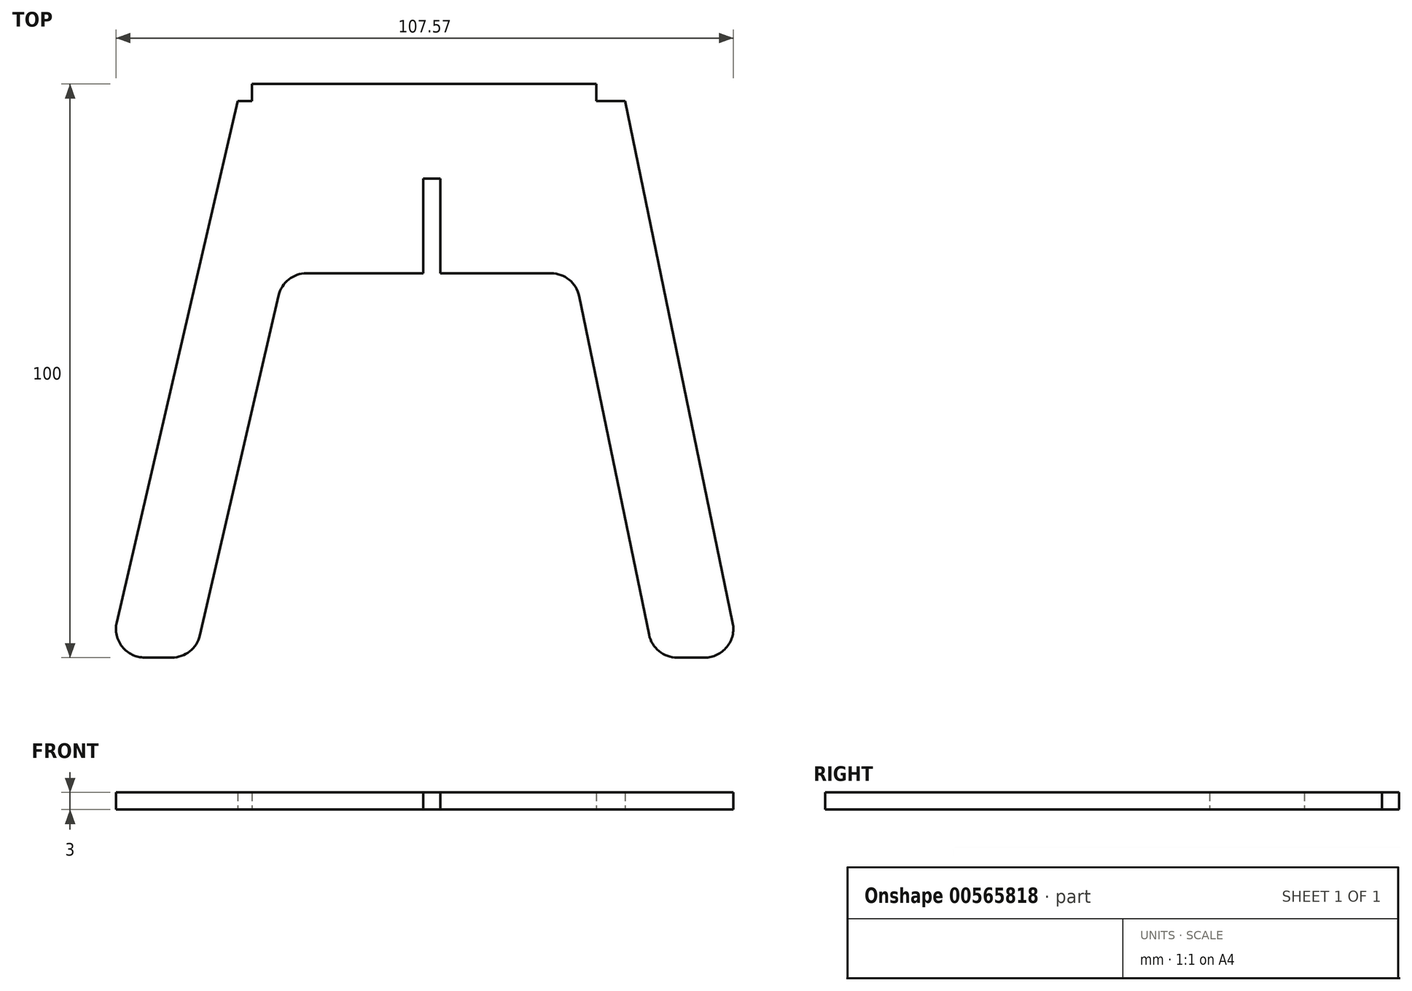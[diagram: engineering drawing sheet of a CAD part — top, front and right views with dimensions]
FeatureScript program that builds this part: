
annotation { "Feature Type Name" : "Feature", "Feature Type Description" : "" }
export const myFeature = defineFeature(function(context is Context, id is Id, definition is map)
    precondition{}
    {
        {
            var Q0;
            Q0=qCreatedBy(makeId("Top.planeOp"),FACE);
            var sketch = newSketch(context, id + "F0", { "sketchPlane" : qUnion([Q0])});
            skLineSegment(sketch, "E0.bottom", {"start": v(-31.33, 50.11) * mm, "end": v(28.67, 50.11) * mm});
            skLineSegment(sketch, "E0.top", {"start": v(-50.03, -49.89) * mm, "end": v(-45.3, -49.89) * mm});
            skPoint(sketch, "E0.middle", {"position": v(0, 0) * mm});
            skLineSegment(sketch, "E1", {"start": v(-33.84, 47.11) * mm, "end": v(-31.33, 47.11) * mm});
            skLineSegment(sketch, "E2", {"start": v(-31.33, 47.11) * mm, "end": v(-31.33, 50.11) * mm});
            skLineSegment(sketch, "E3", {"start": v(28.67, 47.11) * mm, "end": v(28.67, 50.11) * mm});
            skLineSegment(sketch, "E4", {"start": v(-21.82, 17.11) * mm, "end": v(-1.5, 17.11) * mm});
            skLineSegment(sketch, "E5", {"start": v(33.67, 47.11) * mm, "end": v(52.44, -43.88) * mm});
            skLineSegment(sketch, "E6", {"start": v(-54.9, -43.76) * mm, "end": v(-33.84, 47.11) * mm});
            skLineSegment(sketch, "E7", {"start": v(-40.43, -46.02) * mm, "end": v(-26.7, 13.24) * mm});
            skLineSegment(sketch, "E8", {"start": v(25.68, 13.12) * mm, "end": v(37.85, -45.9) * mm});
            skLineSegment(sketch, "E9.trimOffspring", {"start": v(42.75, -49.89) * mm, "end": v(47.54, -49.89) * mm});
            skLineSegment(sketch, "E10.trimOffspring", {"start": v(28.67, 47.11) * mm, "end": v(33.67, 47.11) * mm});
            skPoint(sketch, "E11.visualSharp", {"position": v(-56.33, -49.89) * mm});
            skArc(sketch, "E11.filletArc", {"start": v(-54.9, -43.76) * mm, "mid": v(-53.95, -48) * mm, "end": v(-50.03, -49.89) * mm});
            skPoint(sketch, "E12.visualSharp", {"position": v(38.67, -49.89) * mm});
            skArc(sketch, "E12.filletArc", {"start": v(37.85, -45.9) * mm, "mid": v(39.59, -48.77) * mm, "end": v(42.75, -49.89) * mm});
            skPoint(sketch, "E13.visualSharp", {"position": v(-41.33, -49.89) * mm});
            skArc(sketch, "E13.filletArc", {"start": v(-45.3, -49.89) * mm, "mid": v(-42.19, -48.8) * mm, "end": v(-40.43, -46.02) * mm});
            skPoint(sketch, "E14.visualSharp", {"position": v(53.67, -49.89) * mm});
            skArc(sketch, "E14.filletArc", {"start": v(47.54, -49.89) * mm, "mid": v(51.41, -48.05) * mm, "end": v(52.44, -43.88) * mm});
            skPoint(sketch, "E15.visualSharp", {"position": v(24.86, 17.11) * mm});
            skArc(sketch, "E15.filletArc", {"start": v(25.68, 13.12) * mm, "mid": v(23.94, 15.99) * mm, "end": v(20.79, 17.11) * mm});
            skPoint(sketch, "E16.visualSharp", {"position": v(-25.8, 17.11) * mm});
            skArc(sketch, "E16.filletArc", {"start": v(-21.82, 17.11) * mm, "mid": v(-24.93, 16.03) * mm, "end": v(-26.7, 13.24) * mm});
            skLineSegment(sketch, "E17", {"start": v(0, 50.11) * mm, "end": v(0, 17.11) * mm, "construction": true});
            skLineSegment(sketch, "E18", {"start": v(1.5, 17.11) * mm, "end": v(1.5, 33.61) * mm});
            skPoint(sketch, "E18.endSnap0", {"position": v(0, 33.61) * mm});
            skLineSegment(sketch, "E19.MirrorCS", {"start": v(-1.5, 17.11) * mm, "end": v(-1.5, 33.61) * mm});
            skLineSegment(sketch, "E20", {"start": v(1.5, 33.61) * mm, "end": v(-1.5, 33.61) * mm});
            skLineSegment(sketch, "E21.trimOffspring", {"start": v(1.5, 17.11) * mm, "end": v(20.79, 17.11) * mm});
            skSolve(sketch);
        }
        {
            var Q0;
            Q0 = qSketchRegion(id + "F0", true);
            extrude(context, id + "F1", {"entities" : qUnion([Q0]), "depth" : 3 * mm, "offsetDistance" : 25 * mm});
        }
    });
